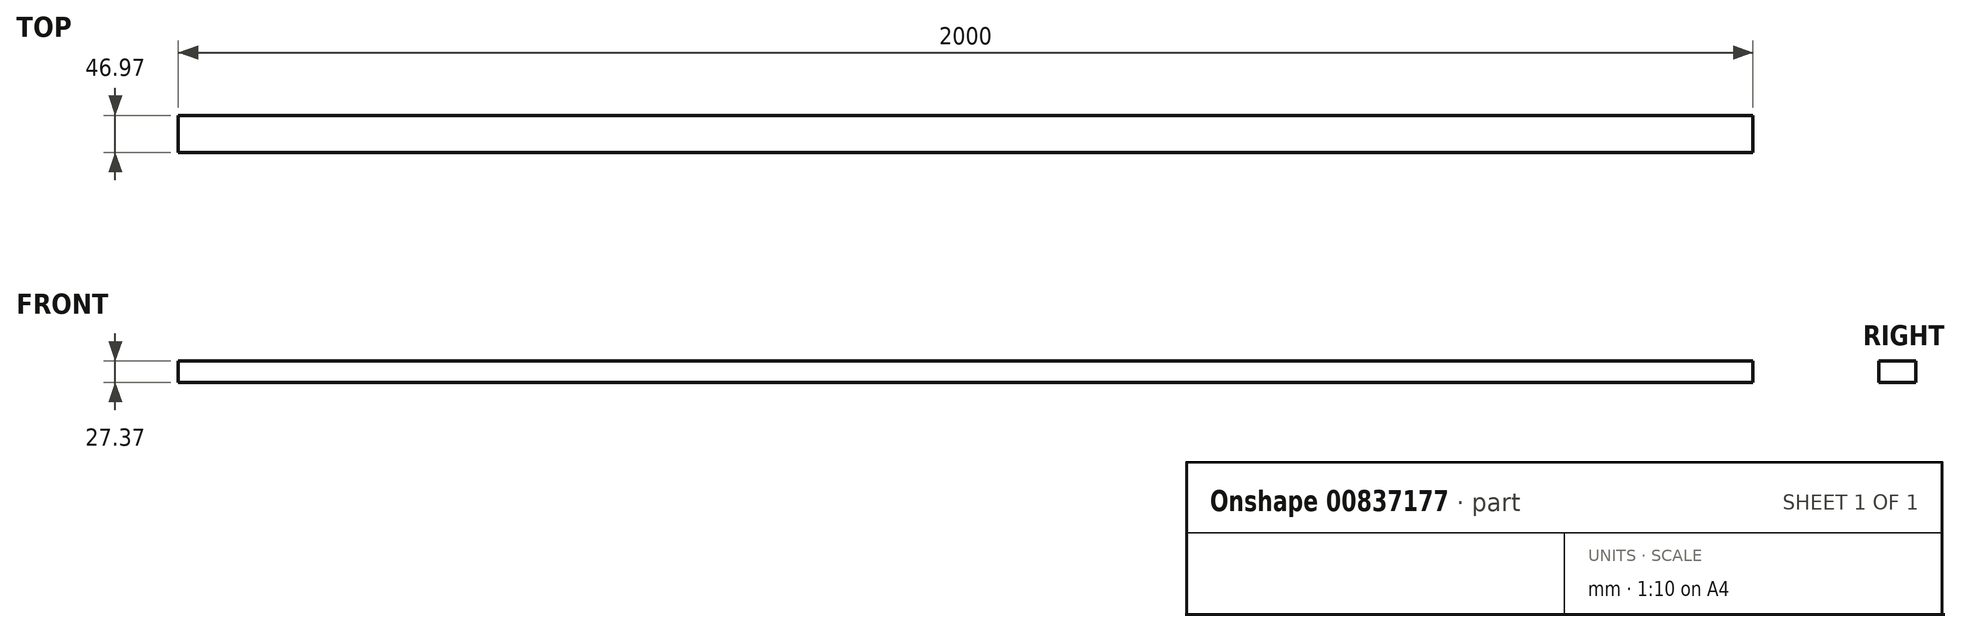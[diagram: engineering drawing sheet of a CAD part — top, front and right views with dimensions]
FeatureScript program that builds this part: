
annotation { "Feature Type Name" : "Feature", "Feature Type Description" : "" }
export const myFeature = defineFeature(function(context is Context, id is Id, definition is map)
    precondition{}
    {
        {
            var Q0;
            Q0=qCreatedBy(makeId("Right.planeOp"),FACE);
            var sketch = newSketch(context, id + "F0", { "sketchPlane" : qUnion([Q0])});
            skLineSegment(sketch, "E0.bottom", {"start": v(0, 0) * mm, "end": v(-46.97, 0) * mm});
            skLineSegment(sketch, "E0.top", {"start": v(0, 27.37) * mm, "end": v(-46.97, 27.37) * mm});
            skLineSegment(sketch, "E0.left", {"start": v(0, 0) * mm, "end": v(0, 27.37) * mm});
            skLineSegment(sketch, "E0.right", {"start": v(-46.97, 0) * mm, "end": v(-46.97, 27.37) * mm});
            skSolve(sketch);
        }
        {
            var Q0;
            Q0 = qSketchRegion(id + "F0", true);
            extrude(context, id + "F1", {"entities" : qUnion([Q0]), "depth" : 2000 * mm, "offsetDistance" : 25 * mm});
        }
    });
